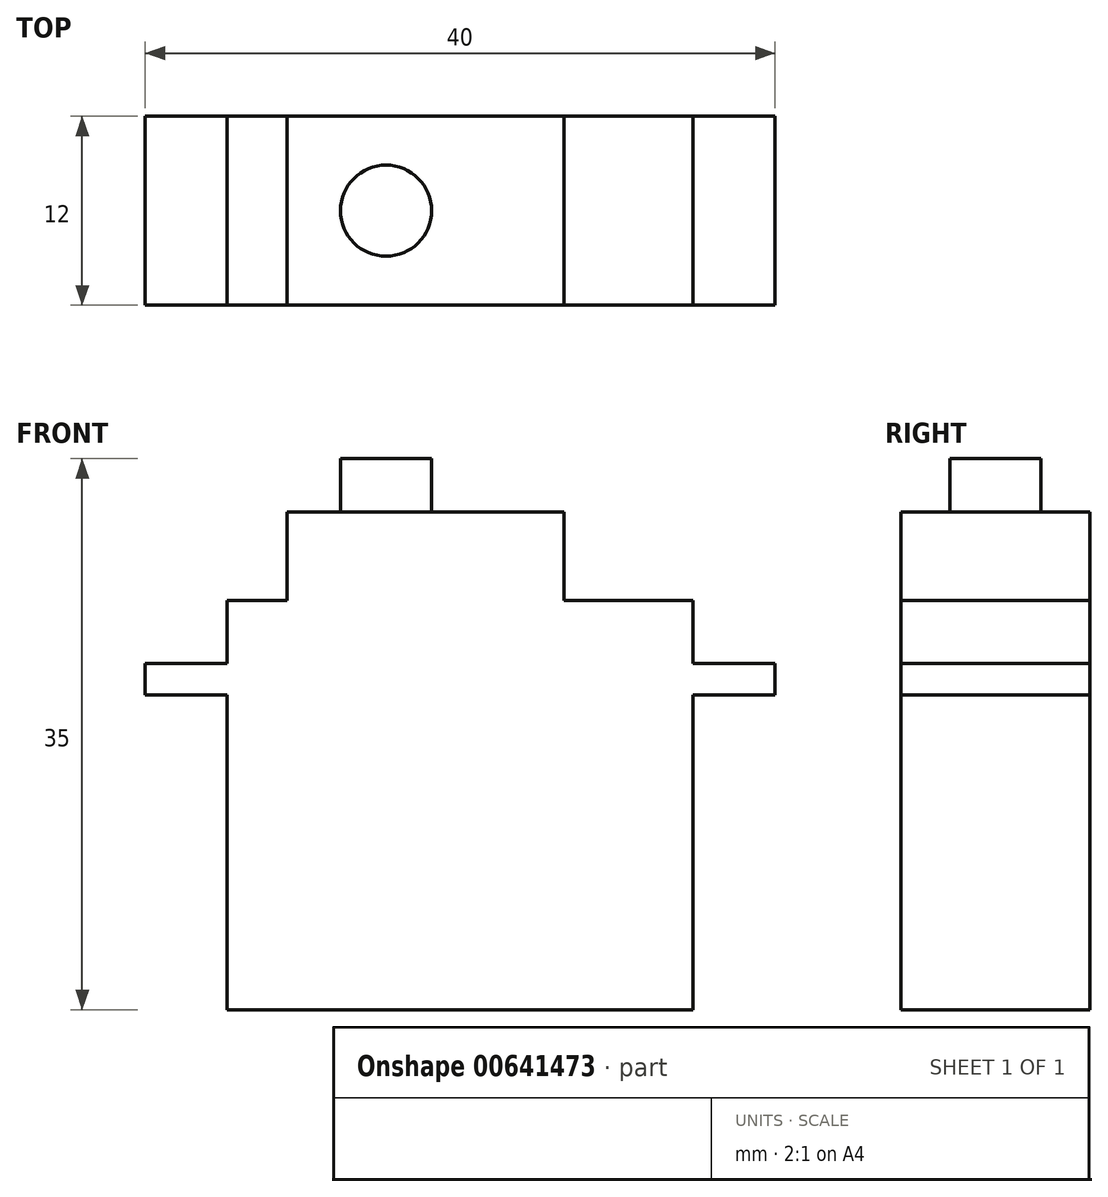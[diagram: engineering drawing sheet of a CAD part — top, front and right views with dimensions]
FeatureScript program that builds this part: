
annotation { "Feature Type Name" : "Feature", "Feature Type Description" : "" }
export const myFeature = defineFeature(function(context is Context, id is Id, definition is map)
    precondition{}
    {
        {
            var Q0;
            Q0=qCreatedBy(makeId("Top.planeOp"),FACE);
            var sketch = newSketch(context, id + "F0", { "sketchPlane" : qUnion([Q0])});
            skLineSegment(sketch, "E0.bottom", {"start": v(14.8, 6) * mm, "end": v(0, 6) * mm});
            skLineSegment(sketch, "E0.top", {"start": v(14.8, -6) * mm, "end": v(0, -6) * mm});
            skLineSegment(sketch, "E0.left", {"start": v(14.8, 6) * mm, "end": v(14.8, -6) * mm});
            skPoint(sketch, "E0.middle", {"position": v(0, 0) * mm});
            skLineSegment(sketch, "E1", {"start": v(0, 6) * mm, "end": v(0, -6) * mm});
            skSolve(sketch);
        }
        {
            var Q0;
            Q0=makeQuery(id+"F0.imprint","IMPRINT",FACE,{"disambiguationData":[TD([[makeQuery(id+"F0.imprint","IMPRINT",EDGE,{"derivedFrom":sQuery(id+"F0.wireOp",EDGE,"E0.bottom")}),1.0]])]});
            extrude(context, id + "F1", {"entities" : qUnion([Q0]), "depth" : 26 * mm, "offsetDistance" : 25 * mm});
        }
        {
            var Q0;
            Q0=makeQuery(id+"F1.opExtrude","SWEPT_FACE",FACE,{"disambiguationData":[OSD([sQuery(id+"F0.wireOp",EDGE,"E0.left")])]});
            var sketch = newSketch(context, id + "F2", { "sketchPlane" : qUnion([Q0])});
            skLineSegment(sketch, "E2.bottom", {"start": v(-6, 20) * mm, "end": v(6, 20) * mm});
            skLineSegment(sketch, "E2.top", {"start": v(-6, 22) * mm, "end": v(6, 22) * mm});
            skLineSegment(sketch, "E2.left", {"start": v(-6, 20) * mm, "end": v(-6, 22) * mm});
            skLineSegment(sketch, "E2.right", {"start": v(6, 20) * mm, "end": v(6, 22) * mm});
            skSolve(sketch);
        }
        {
            var Q0;
            Q0=makeQuery(id+"F2.imprint","IMPRINT",FACE,{"disambiguationData":[TD([[makeQuery(id+"F2.imprint","IMPRINT",EDGE,{"derivedFrom":sQuery(id+"F2.wireOp",EDGE,"E2.bottom")}),1.0]])]});
            extrude(context, id + "F3", {"entities" : qUnion([Q0]), "operationType" : NewBodyOperationType.ADD, "depth" : 5.2 * mm, "offsetDistance" : 25 * mm});
        }
        {
            var Q0;
            Q0=makeQuery(id+"F1.opExtrude","SWEPT_BODY",BODY,{"disambiguationData":[OSD([sQuery(id+"F0.wireOp",EDGE,"E0.bottom"),sQuery(id+"F0.wireOp",EDGE,"E0.top"),sQuery(id+"F0.wireOp",EDGE,"E0.left"),sQuery(id+"F0.wireOp",EDGE,"E1")])]});
            var Q1;
            Q1=qCreatedBy(makeId("Right.planeOp"),FACE);
            mirror(context, id + "F4", {"operationType" : NewBodyOperationType.ADD, "entities" : qUnion([Q0]), "mirrorPlane" : qUnion([Q1])});
        }
        {
            var Q0;
            {var subQ0=makeQuery(id+"F1.opExtrude","CAP_FACE",FACE,{"disambiguationData":[OSD([sQuery(id+"F0.wireOp",EDGE,"E0.bottom"),sQuery(id+"F0.wireOp",EDGE,"E0.top"),sQuery(id+"F0.wireOp",EDGE,"E0.left"),sQuery(id+"F0.wireOp",EDGE,"E1")])],"isStart":false});Q0=makeQuery(id+"F4.boolean.opBoolean","MERGE",FACE,{"derivedFrom":[subQ0,makeQuery(id+"F4.opPattern","COPY",FACE,{"derivedFrom":subQ0,"instanceName":"1"})]});}
            var sketch = newSketch(context, id + "F5", { "sketchPlane" : qUnion([Q0])});
            skLineSegment(sketch, "E3.bottom", {"start": v(-11, 6) * mm, "end": v(6.6, 6) * mm});
            skLineSegment(sketch, "E3.top", {"start": v(-11, -6) * mm, "end": v(6.6, -6) * mm});
            skLineSegment(sketch, "E3.left", {"start": v(-11, 6) * mm, "end": v(-11, -6) * mm});
            skLineSegment(sketch, "E3.right", {"start": v(6.6, 6) * mm, "end": v(6.6, -6) * mm});
            skSolve(sketch);
        }
        {
            var Q0;
            Q0=makeQuery(id+"F5.imprint","IMPRINT",FACE,{"disambiguationData":[TD([[makeQuery(id+"F5.imprint","IMPRINT",EDGE,{"derivedFrom":sQuery(id+"F5.wireOp",EDGE,"E3.bottom")}),1.0]])]});
            extrude(context, id + "F6", {"entities" : qUnion([Q0]), "operationType" : NewBodyOperationType.ADD, "depth" : 5.6 * mm, "offsetDistance" : 25 * mm});
        }
        {
            var Q0;
            Q0=makeQuery(id+"F6.opExtrude","CAP_FACE",FACE,{"disambiguationData":[OSD([sQuery(id+"F5.wireOp",EDGE,"E3.bottom"),sQuery(id+"F5.wireOp",EDGE,"E3.top"),sQuery(id+"F5.wireOp",EDGE,"E3.left"),sQuery(id+"F5.wireOp",EDGE,"E3.right")])],"isStart":false});
            var sketch = newSketch(context, id + "F7", { "sketchPlane" : qUnion([Q0])});
            skCircle(sketch, "E4", {"center": v(-4.7, 0) * mm, "radius": 2.9 * mm});
            skSolve(sketch);
        }
        {
            var Q0;
            Q0=makeQuery(id+"F7.imprint","IMPRINT",FACE,{"disambiguationData":[TD([[makeQuery(id+"F7.imprint","IMPRINT",EDGE,{"derivedFrom":sQuery(id+"F7.wireOp",EDGE,"E4")}),1.0]])]});
            extrude(context, id + "F8", {"entities" : qUnion([Q0]), "operationType" : NewBodyOperationType.ADD, "depth" : 3.4 * mm, "offsetDistance" : 25 * mm});
        }
    });
